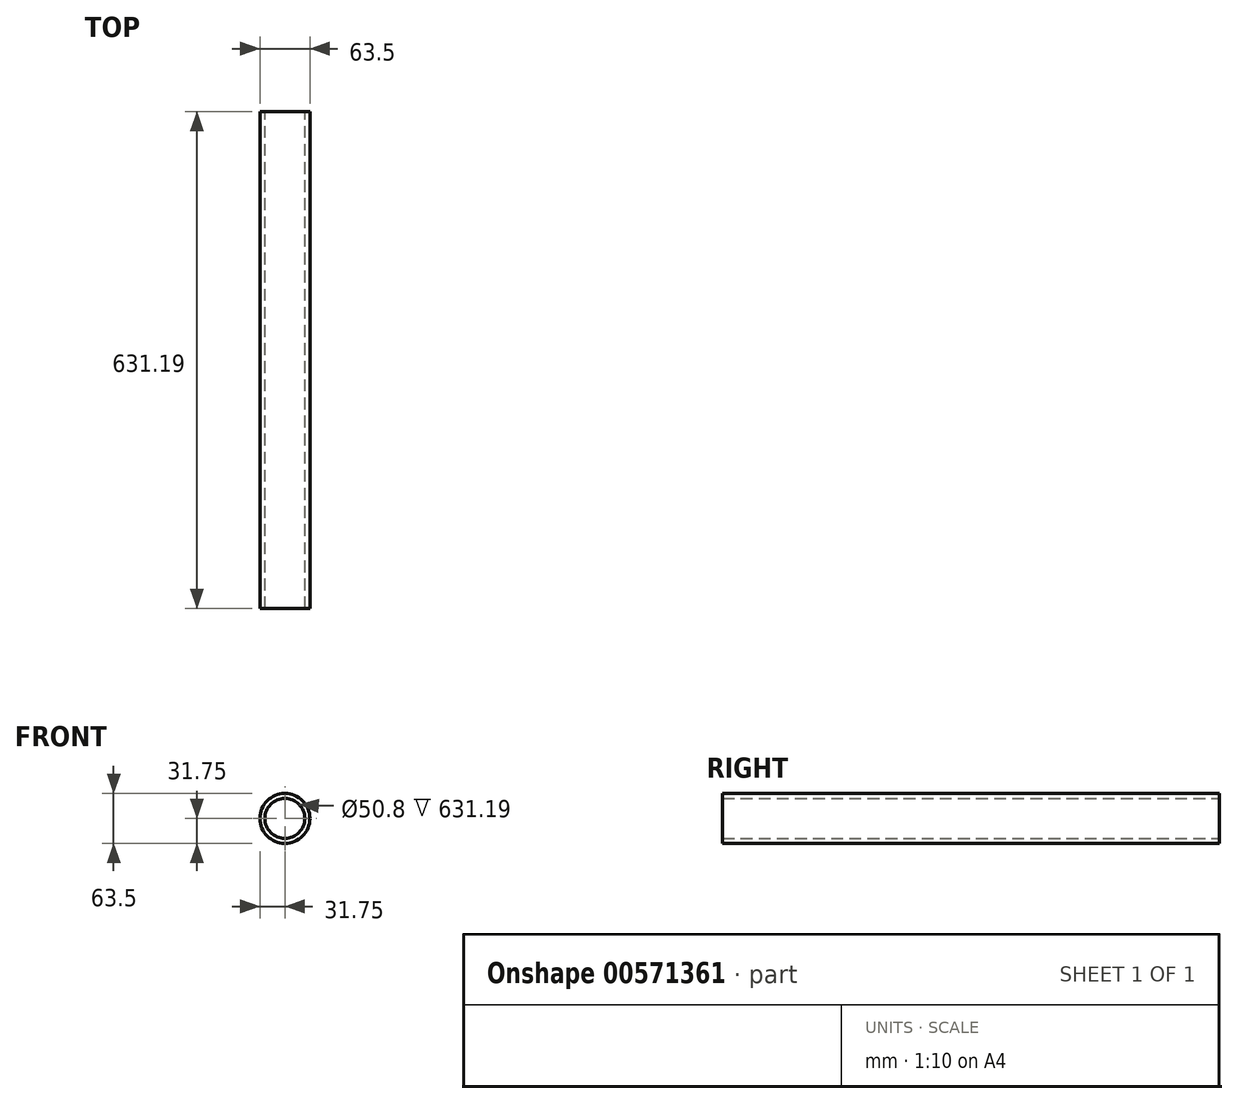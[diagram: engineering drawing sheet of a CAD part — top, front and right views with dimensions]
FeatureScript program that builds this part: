
annotation { "Feature Type Name" : "Feature", "Feature Type Description" : "" }
export const myFeature = defineFeature(function(context is Context, id is Id, definition is map)
    precondition{}
    {
        {
            var Q0;
            Q0=qCreatedBy(makeId("Front.planeOp"),FACE);
            var sketch = newSketch(context, id + "F0", { "sketchPlane" : qUnion([Q0])});
            skCircle(sketch, "E0", {"center": v(0, 0) * mm, "radius": 31.75 * mm});
            skSolve(sketch);
        }
        {
            var Q0;
            Q0=makeQuery(id+"F0.imprint","IMPRINT",FACE,{"disambiguationData":[TD([[makeQuery(id+"F0.imprint","IMPRINT",EDGE,{"derivedFrom":sQuery(id+"F0.wireOp",EDGE,"E0")}),1.0]])]});
            extrude(context, id + "F1", {"entities" : qUnion([Q0]), "depth" : 304.8 * mm, "offsetDistance" : 25.4 * mm});
        }
        {
            var Q0;
            Q0=makeQuery(id+"F1.opExtrude","CAP_FACE",FACE,{"disambiguationData":[OSD([sQuery(id+"F0.wireOp",EDGE,"E0")])],"isStart":true});
            var sketch = newSketch(context, id + "F2", { "sketchPlane" : qUnion([Q0])});
            skCircle(sketch, "E1", {"center": v(0, 0) * mm, "radius": 25.4 * mm});
            skSolve(sketch);
        }
        {
            var Q0;
            Q0=makeQuery(id+"F2.imprint","IMPRINT",FACE,{"disambiguationData":[TD([[makeQuery(id+"F2.imprint","IMPRINT",EDGE,{"derivedFrom":sQuery(id+"F2.wireOp",EDGE,"E1")}),1.0]])]});
            extrude(context, id + "F3", {"entities" : qUnion([Q0]), "operationType" : NewBodyOperationType.REMOVE, "oppositeDirection" : true, "depth" : 304.8 * mm, "offsetDistance" : 25.4 * mm});
        }
        {
            var Q0;
            Q0=makeQuery(id+"F1.opExtrude","CAP_FACE",FACE,{"disambiguationData":[OSD([sQuery(id+"F0.wireOp",EDGE,"E0")])],"isStart":false});
            extrude(context, id + "F4", {"entities" : qUnion([Q0]), "operationType" : NewBodyOperationType.ADD, "depth" : 326.4 * mm, "offsetDistance" : 25.4 * mm});
        }
    });
